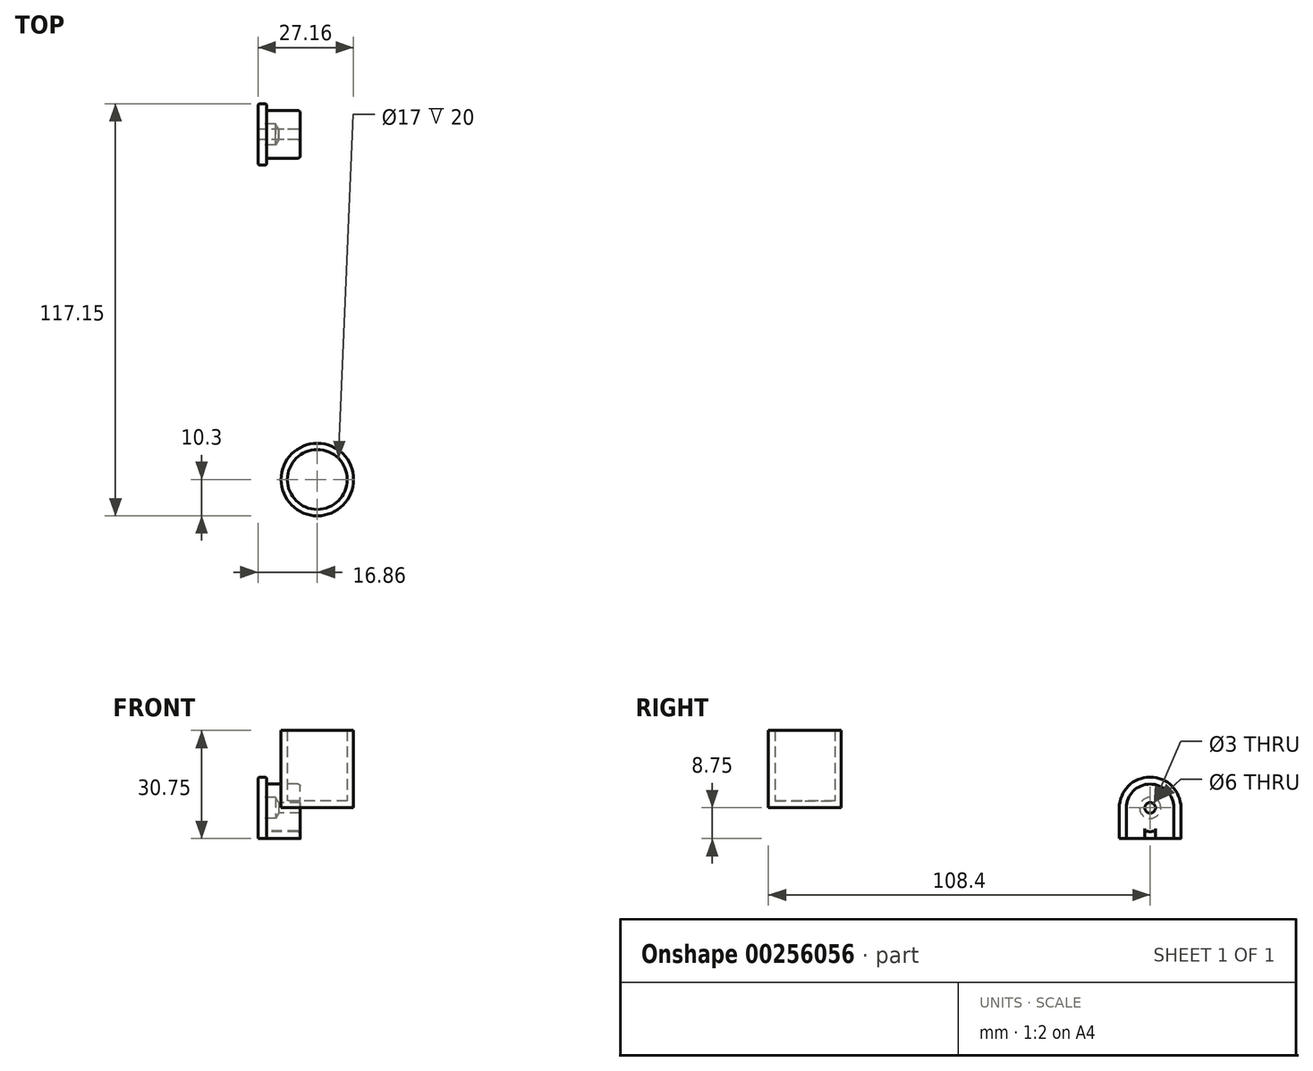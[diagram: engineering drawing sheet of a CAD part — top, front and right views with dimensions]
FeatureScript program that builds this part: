
annotation { "Feature Type Name" : "Feature", "Feature Type Description" : "" }
export const myFeature = defineFeature(function(context is Context, id is Id, definition is map)
    precondition{}
    {
        {
            var Q0;
            Q0=qCreatedBy(makeId("Top.planeOp"),FACE);
            var sketch = newSketch(context, id + "F0", { "sketchPlane" : qUnion([Q0])});
            skCircle(sketch, "E0", {"center": v(0, 0) * mm, "radius": 8.5 * mm});
            skCircle(sketch, "E1", {"center": v(0, 0) * mm, "radius": 10.3 * mm});
            skLineSegment(sketch, "E2.bottom", {"start": v(-4.86, 91.35) * mm, "end": v(-14.36, 91.35) * mm});
            skLineSegment(sketch, "E2.top", {"start": v(-4.86, 104.85) * mm, "end": v(-14.36, 104.85) * mm});
            skLineSegment(sketch, "E2.left", {"start": v(-4.86, 91.35) * mm, "end": v(-4.86, 104.85) * mm});
            skLineSegment(sketch, "E2.right", {"start": v(-14.36, 91.35) * mm, "end": v(-14.36, 104.85) * mm});
            skPoint(sketch, "E2.middle", {"position": v(-9.6, 98.1) * mm});
            skLineSegment(sketch, "E3.bottom", {"start": v(-14.36, 89.35) * mm, "end": v(-16.86, 89.35) * mm});
            skLineSegment(sketch, "E3.top", {"start": v(-14.36, 106.85) * mm, "end": v(-16.86, 106.85) * mm});
            skLineSegment(sketch, "E3.left", {"start": v(-14.36, 89.35) * mm, "end": v(-14.36, 106.85) * mm});
            skLineSegment(sketch, "E3.right", {"start": v(-16.86, 89.35) * mm, "end": v(-16.86, 106.85) * mm});
            skPoint(sketch, "E3.middle", {"position": v(-15.6, 98.1) * mm});
            skLineSegment(sketch, "E4", {"start": v(-16.86, 98.1) * mm, "end": v(-4.86, 98.1) * mm, "construction": true});
            skLineSegment(sketch, "E5.bottom", {"start": v(-4.86, 96.6) * mm, "end": v(-16.86, 96.6) * mm});
            skLineSegment(sketch, "E5.top", {"start": v(-4.86, 99.6) * mm, "end": v(-16.86, 99.6) * mm});
            skLineSegment(sketch, "E5.left", {"start": v(-4.86, 96.6) * mm, "end": v(-4.86, 99.6) * mm});
            skLineSegment(sketch, "E5.right", {"start": v(-16.86, 96.6) * mm, "end": v(-16.86, 99.6) * mm});
            skPoint(sketch, "E5.middle", {"position": v(-10.86, 98.1) * mm});
            skLineSegment(sketch, "E6", {"start": v(-16.86, 98.1) * mm, "end": v(-4.86, 98.1) * mm});
            skSolve(sketch);
        }
        {
            var Q0;
            Q0=makeQuery(id+"F0.imprint","IMPRINT",FACE,{"disambiguationData":[TD([[makeQuery(id+"F0.imprint","IMPRINT",EDGE,{"derivedFrom":sQuery(id+"F0.wireOp",EDGE,"E0")}),1.0]])]});
            extrude(context, id + "F1", {"entities" : qUnion([Q0]), "depth" : 2 * mm});
        }
        {
            var Q0;
            Q0=makeQuery(id+"F0.imprint","IMPRINT",FACE,{"disambiguationData":[TD([[makeQuery(id+"F0.imprint","IMPRINT",EDGE,{"derivedFrom":sQuery(id+"F0.wireOp",EDGE,"E0")}),-1.0]])]});
            extrude(context, id + "F2", {"entities" : qUnion([Q0]), "operationType" : NewBodyOperationType.ADD, "depth" : 22 * mm});
        }
        {
            var Q0;
            {var subQ0=sQuery(id+"F0.wireOp",EDGE,"E2.top");Q0=makeQuery(id+"F0.imprint","IMPRINT",FACE,{"disambiguationData":[TD([[makeQuery(id+"F0.imprint","IMPRINT",EDGE,{"derivedFrom":subQ0}),1.0]])]});}
            var Q1;
            {var subQ1=sQuery(id+"F0.wireOp",EDGE,"E3.top");Q1=makeQuery(id+"F0.imprint","IMPRINT",FACE,{"disambiguationData":[TD([[makeQuery(id+"F0.imprint","IMPRINT",EDGE,{"derivedFrom":subQ1}),1.0]])]});}
            var Q2;
            {var subQ5=sQuery(id+"F0.wireOp",EDGE,"E5.right");Q2=makeQuery(id+"F0.imprint","IMPRINT",FACE,{"disambiguationData":[TD([[makeQuery(id+"F0.imprint","IMPRINT",EDGE,{"derivedFrom":subQ5}),-1.0]])]});}
            var Q3;
            {var subQ5=sQuery(id+"F0.wireOp",EDGE,"E5.left");Q3=makeQuery(id+"F0.imprint","IMPRINT",FACE,{"disambiguationData":[TD([[makeQuery(id+"F0.imprint","IMPRINT",EDGE,{"derivedFrom":subQ5}),1.0]])]});}
            var Q4;
            {var subQ0=sQuery(id+"F0.wireOp",EDGE,"E2.bottom");Q4=makeQuery(id+"F0.imprint","IMPRINT",FACE,{"disambiguationData":[TD([[makeQuery(id+"F0.imprint","IMPRINT",EDGE,{"derivedFrom":subQ0}),-1.0]])]});}
            var Q5;
            {var subQ1=sQuery(id+"F0.wireOp",EDGE,"E3.bottom");Q5=makeQuery(id+"F0.imprint","IMPRINT",FACE,{"disambiguationData":[TD([[makeQuery(id+"F0.imprint","IMPRINT",EDGE,{"derivedFrom":subQ1}),-1.0]])]});}
            extrude(context, id + "F3", {"entities" : qUnion([Q0, Q1, Q2, Q3, Q4, Q5]), "oppositeDirection" : true, "depth" : (17.5 / 2) * mm});
        }
        {
            var Q0;
            {var subQ0=sQuery(id+"F0.wireOp",EDGE,"E5.bottom");var subQ1=sQuery(id+"F0.wireOp",EDGE,"E3.left");var subQ2=makeQuery(id+"F0.imprint","INTERSECT",VERTEX,{"derivedFrom":[subQ1,subQ0]});Q0=makeQuery(id+"F0.imprint","IMPRINT",FACE,{"disambiguationData":[TD([[makeQuery(id+"F0.imprint","IMPRINT",EDGE,{"disambiguationData":[TD([[subQ2,-1.0]])],"derivedFrom":subQ1}),-1.0]])]});}
            var Q1;
            {var subQ0=sQuery(id+"F0.wireOp",EDGE,"E5.bottom");var subQ1=sQuery(id+"F0.wireOp",EDGE,"E3.left");var subQ2=makeQuery(id+"F0.imprint","INTERSECT",VERTEX,{"derivedFrom":[subQ1,subQ0]});Q1=makeQuery(id+"F0.imprint","IMPRINT",FACE,{"disambiguationData":[TD([[makeQuery(id+"F0.imprint","IMPRINT",EDGE,{"disambiguationData":[TD([[subQ2,-1.0]])],"derivedFrom":subQ1}),1.0]])]});}
            var Q2;
            {var subQ1=sQuery(id+"F0.wireOp",EDGE,"E3.bottom");Q2=makeQuery(id+"F0.imprint","IMPRINT",FACE,{"disambiguationData":[TD([[makeQuery(id+"F0.imprint","IMPRINT",EDGE,{"derivedFrom":subQ1}),-1.0]])]});}
            var Q3;
            {var subQ0=sQuery(id+"F0.wireOp",EDGE,"E2.bottom");Q3=makeQuery(id+"F0.imprint","IMPRINT",FACE,{"disambiguationData":[TD([[makeQuery(id+"F0.imprint","IMPRINT",EDGE,{"derivedFrom":subQ0}),-1.0]])]});}
            var Q4;
            Q4=sQuery(id+"F0.wireOp",EDGE,"E6");
            revolve(context, id + "F4", {"operationType" : NewBodyOperationType.ADD, "entities" : qUnion([Q0, Q1, Q2, Q3]), "axis" : qUnion([Q4]), "revolveType" : RevolveType.FULL});
        }
        {
            var Q0;
            {var subQ0=sQuery(id+"F0.wireOp",EDGE,"E5.right");var subQ1=sQuery(id+"F0.wireOp",EDGE,"E3.right");Q0=makeQuery(id+"F4.boolean.opBoolean","MERGE",FACE,{"derivedFrom":[makeQuery(id+"F3.opExtrude","SWEPT_FACE",FACE,{"disambiguationData":[OSD([subQ1,subQ0])]}),makeQuery(id+"F4.opRevolve","SWEPT_FACE",FACE,{"disambiguationData":[OSD([subQ1,subQ0])]})]});}
            var sketch = newSketch(context, id + "F5", { "sketchPlane" : qUnion([Q0])});
            skPoint(sketch, "E7.0", {"position": v(-98.1, 0) * mm});
            skPoint(sketch, "E8.0", {"position": v(-96.6, 0) * mm});
            skCircle(sketch, "E9", {"center": v(-98.1, 0) * mm, "radius": 1.5 * mm});
            skSolve(sketch);
        }
        {
            var Q0;
            Q0=makeQuery(id+"F5.imprint","IMPRINT",FACE,{"disambiguationData":[TD([[makeQuery(id+"F5.imprint","IMPRINT",EDGE,{"derivedFrom":sQuery(id+"F5.wireOp",EDGE,"E9")}),1.0]])]});
            extrude(context, id + "F6", {"entities" : qUnion([Q0]), "operationType" : NewBodyOperationType.REMOVE, "endBound" : BoundingType.THROUGH_ALL, "oppositeDirection" : true, "depth" : 25 * mm});
        }
        {
            var Q0;
            Q0=makeQuery(id+"F4.opRevolve","SWEPT_EDGE",EDGE,{"disambiguationData":[OSD([sQuery(id+"F0.wireOp",EDGE,"E3.bottom"),sQuery(id+"F0.wireOp",EDGE,"E3.right")])]});
            var Q1;
            Q1=makeQuery(id+"F3.opExtrude","SWEPT_EDGE",EDGE,{"disambiguationData":[OSD([sQuery(id+"F0.wireOp",EDGE,"E3.bottom"),sQuery(id+"F0.wireOp",EDGE,"E3.right")])]});
            var Q2;
            Q2=makeQuery(id+"F3.opExtrude","SWEPT_EDGE",EDGE,{"disambiguationData":[OSD([sQuery(id+"F0.wireOp",EDGE,"E3.top"),sQuery(id+"F0.wireOp",EDGE,"E3.right")])]});
            var Q3;
            Q3=makeQuery(id+"F4.opRevolve","SWEPT_EDGE",EDGE,{"disambiguationData":[OSD([sQuery(id+"F0.wireOp",EDGE,"E3.bottom"),sQuery(id+"F0.wireOp",EDGE,"E3.left")])]});
            var Q4;
            Q4=makeQuery(id+"F3.opExtrude","SWEPT_EDGE",EDGE,{"disambiguationData":[OSD([sQuery(id+"F0.wireOp",EDGE,"E3.bottom"),sQuery(id+"F0.wireOp",EDGE,"E3.left")])]});
            var Q5;
            Q5=makeQuery(id+"F3.opExtrude","SWEPT_EDGE",EDGE,{"disambiguationData":[OSD([sQuery(id+"F0.wireOp",EDGE,"E3.top"),sQuery(id+"F0.wireOp",EDGE,"E3.left")])]});
            var Q6;
            Q6=makeQuery(id+"F3.opExtrude","SWEPT_EDGE",EDGE,{"disambiguationData":[OSD([sQuery(id+"F0.wireOp",EDGE,"E2.bottom"),sQuery(id+"F0.wireOp",EDGE,"E2.left")])]});
            var Q7;
            Q7=makeQuery(id+"F4.opRevolve","SWEPT_EDGE",EDGE,{"disambiguationData":[OSD([sQuery(id+"F0.wireOp",EDGE,"E2.bottom"),sQuery(id+"F0.wireOp",EDGE,"E2.left")])]});
            var Q8;
            Q8=makeQuery(id+"F3.opExtrude","SWEPT_EDGE",EDGE,{"disambiguationData":[OSD([sQuery(id+"F0.wireOp",EDGE,"E2.top"),sQuery(id+"F0.wireOp",EDGE,"E2.left")])]});
            fillet(context, id + "F7", {"entities" : qUnion([Q0, Q1, Q2, Q3, Q4, Q5, Q6, Q7, Q8]), "radius" : 0.6 * mm, "tangentPropagation" : true, "allowEdgeOverflow" : false});
        }
        {
            var Q0;
            Q0=sQuery(id+"F5.wireOp",VERTEX,"E7.0");
            var Q1;
            Q1=makeQuery(id+"F3.opExtrude","SWEPT_BODY",BODY,{"disambiguationData":[OSD([sQuery(id+"F0.wireOp",EDGE,"E2.bottom"),sQuery(id+"F0.wireOp",EDGE,"E2.top"),sQuery(id+"F0.wireOp",EDGE,"E2.left"),sQuery(id+"F0.wireOp",EDGE,"E3.bottom"),sQuery(id+"F0.wireOp",EDGE,"E3.top"),sQuery(id+"F0.wireOp",EDGE,"E3.left"),sQuery(id+"F0.wireOp",EDGE,"E3.right"),sQuery(id+"F0.wireOp",EDGE,"E5.left"),sQuery(id+"F0.wireOp",EDGE,"E5.right")])]});
            hole(context, id + "F8", {"style" : HoleStyle.SIMPLE, "endStyle" : HoleEndStyle.BLIND, "holeDiameter" : 6 * mm, "holeDepth" : 5 * mm, "tappedDepth" : 12 * mm, "tapClearance" : 3, "startFromSketch" : true, "locations" : qUnion([Q0]), "scope" : qUnion([Q1])});
        }
    });
